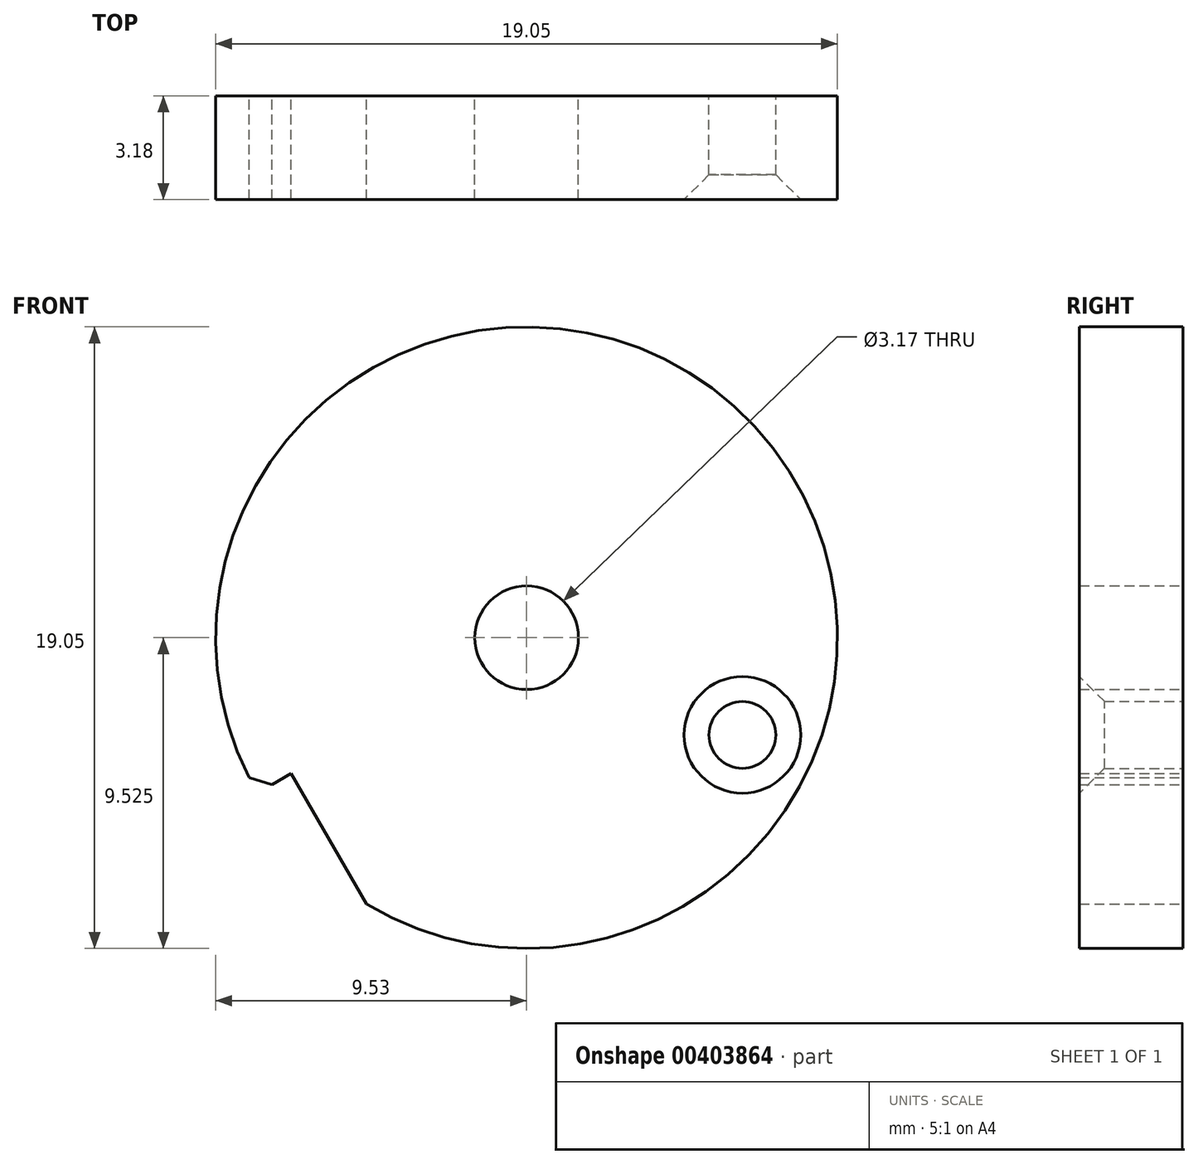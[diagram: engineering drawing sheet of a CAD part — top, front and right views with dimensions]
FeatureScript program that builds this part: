
annotation { "Feature Type Name" : "Feature", "Feature Type Description" : "" }
export const myFeature = defineFeature(function(context is Context, id is Id, definition is map)
    precondition{}
    {
        {
            var Q0;
            Q0=qCreatedBy(makeId("Front.planeOp"),FACE);
            var sketch = newSketch(context, id + "F0", { "sketchPlane" : qUnion([Q0])});
            skCircle(sketch, "E0", {"center": v(1.32, 2.6) * mm, "radius": 1.59 * mm});
            skCircle(sketch, "E1", {"center": v(7.93, -0.37) * mm, "radius": 1.02 * mm});
            skLineSegment(sketch, "E2", {"start": v(-5.9, -1.56) * mm, "end": v(-3.6, -5.56) * mm});
            skLineSegment(sketch, "E3.trimOffspring", {"start": v(-5.9, -1.56) * mm, "end": v(-6.93, -2.15) * mm});
            skArc(sketch, "E4", {"start": v(-3.6, -5.56) * mm, "mid": v(8.12, 9.28) * mm, "end": v(-6.93, -2.15) * mm});
            skSolve(sketch);
        }
        {
            var Q0;
            Q0=makeQuery(id+"F0.imprint","IMPRINT",FACE,{"disambiguationData":[TD([[makeQuery(id+"F0.imprint","IMPRINT",EDGE,{"derivedFrom":sQuery(id+"F0.wireOp",EDGE,"E0")}),-1.0]])]});
            extrude(context, id + "F1", {"entities" : qUnion([Q0]), "endBound" : BoundingType.SYMMETRIC, "depth" : 3.17 * mm});
        }
        {
            var Q0;
            Q0=makeQuery(id+"F1.opExtrude","CAP_EDGE",EDGE,{"disambiguationData":[OSD([sQuery(id+"F0.wireOp",EDGE,"E1")])],"isStart":false});
            chamfer(context, id + "F2", {"entities" : qUnion([Q0]), "chamferType" : ChamferType.TWO_OFFSETS, "width1" : 0.76 * mm, "oppositeDirection" : false, "width2" : 0.76 * mm, "tangentPropagation" : true});
        }
        {
            var Q0;
            Q0=makeQuery(id+"F1.opExtrude","SWEPT_EDGE",EDGE,{"disambiguationData":[OSD([sQuery(id+"F0.wireOp",EDGE,"E3.trimOffspring"),sQuery(id+"F0.wireOp",EDGE,"E4")])]});
            chamfer(context, id + "F3", {"entities" : qUnion([Q0]), "width" : 0.5 * mm, "tangentPropagation" : true});
        }
    });
